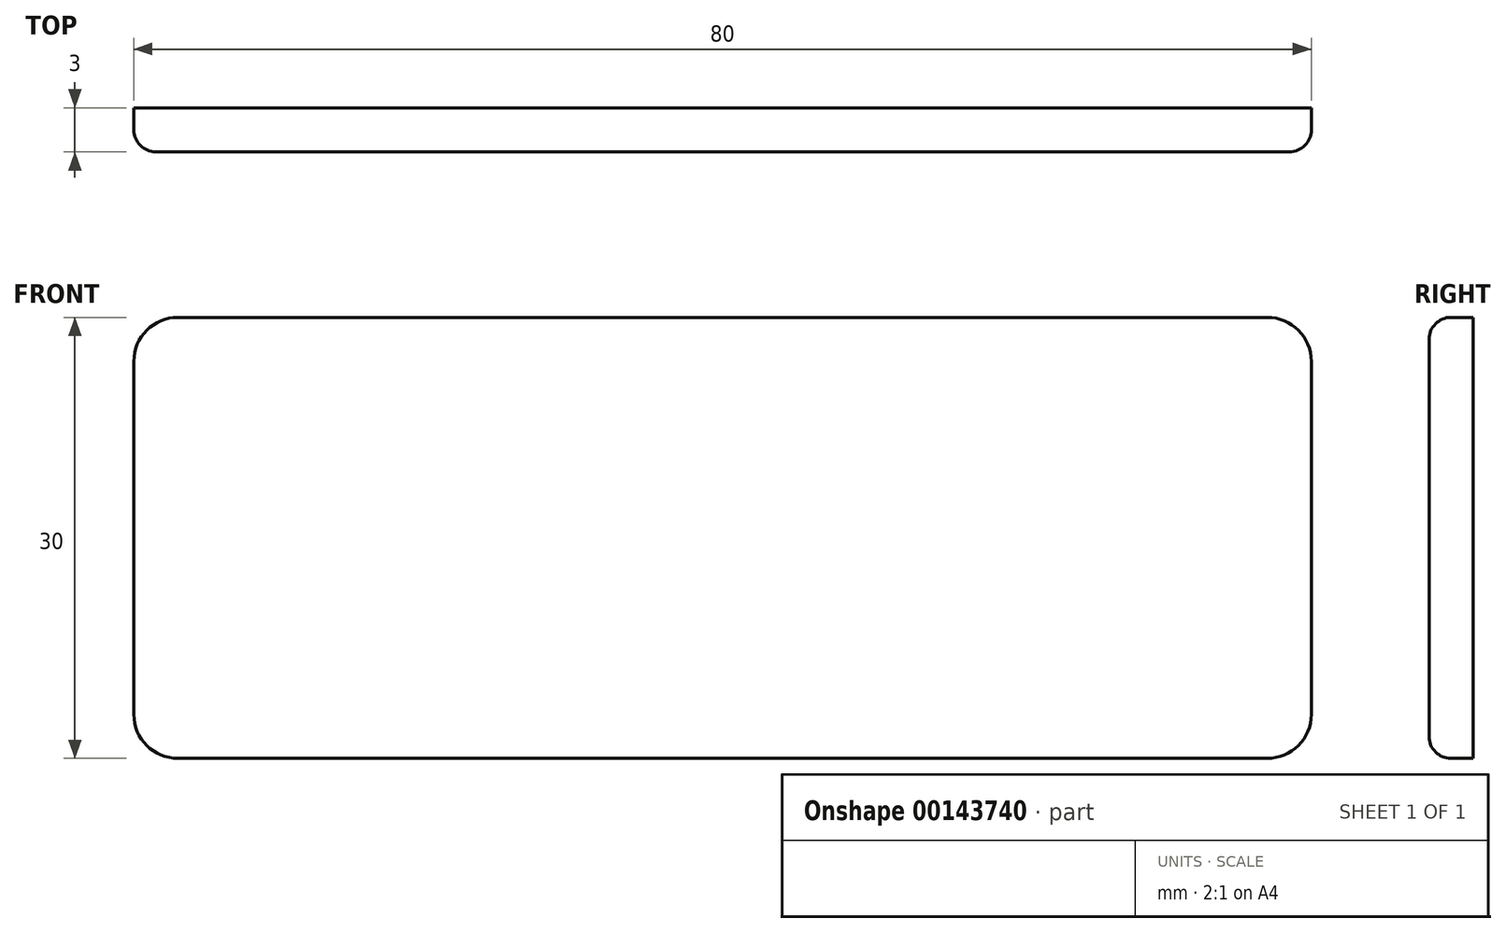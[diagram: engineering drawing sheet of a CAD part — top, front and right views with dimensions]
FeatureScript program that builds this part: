
annotation { "Feature Type Name" : "Feature", "Feature Type Description" : "" }
export const myFeature = defineFeature(function(context is Context, id is Id, definition is map)
    precondition{}
    {
        {
            var Q0;
            Q0=qCreatedBy(makeId("Front.planeOp"),FACE);
            var sketch = newSketch(context, id + "F0", { "sketchPlane" : qUnion([Q0])});
            skLineSegment(sketch, "E0.bottom", {"start": v(37, -15) * mm, "end": v(-37, -15) * mm});
            skLineSegment(sketch, "E0.top", {"start": v(37, 15) * mm, "end": v(-37, 15) * mm});
            skLineSegment(sketch, "E0.left", {"start": v(40, -12) * mm, "end": v(40, 12) * mm});
            skLineSegment(sketch, "E0.right", {"start": v(-40, -12) * mm, "end": v(-40, 12) * mm});
            skPoint(sketch, "E0.middle", {"position": v(0, 0) * mm});
            skPoint(sketch, "E1.visualSharp", {"position": v(-40, 15) * mm});
            skArc(sketch, "E1.filletArc", {"start": v(-37, 15) * mm, "mid": v(-39.12, 14.12) * mm, "end": v(-40, 12) * mm});
            skPoint(sketch, "E2.visualSharp", {"position": v(40, 15) * mm});
            skArc(sketch, "E2.filletArc", {"start": v(40, 12) * mm, "mid": v(39.12, 14.12) * mm, "end": v(37, 15) * mm});
            skPoint(sketch, "E3.visualSharp", {"position": v(40, -15) * mm});
            skArc(sketch, "E3.filletArc", {"start": v(37, -15) * mm, "mid": v(39.12, -14.12) * mm, "end": v(40, -12) * mm});
            skPoint(sketch, "E4.visualSharp", {"position": v(-40, -15) * mm});
            skArc(sketch, "E4.filletArc", {"start": v(-40, -12) * mm, "mid": v(-39.12, -14.12) * mm, "end": v(-37, -15) * mm});
            skSolve(sketch);
        }
        {
            var Q0;
            Q0 = qSketchRegion(id + "F0", true);
            extrude(context, id + "F1", {"entities" : qUnion([Q0]), "depth" : 3 * mm});
        }
        {
            var Q0;
            Q0=makeQuery(id+"F1.opExtrude","CAP_EDGE",EDGE,{"disambiguationData":[OSD([sQuery(id+"F0.wireOp",EDGE,"E0.bottom")])],"isStart":false});
            fillet(context, id + "F2", {"entities" : qUnion([Q0]), "radius" : 1.5 * mm, "tangentPropagation" : true, "allowEdgeOverflow" : false});
        }
    });
